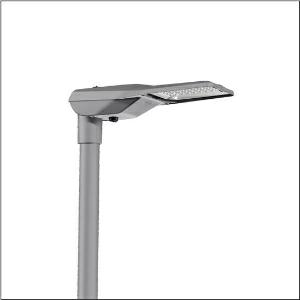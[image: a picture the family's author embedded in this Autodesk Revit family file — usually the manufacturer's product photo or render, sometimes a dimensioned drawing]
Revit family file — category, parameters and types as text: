
# Revit family: streetlight_sl_21_iq_mini___st1_0ab_5xe2m31y08gb_c9fc
name_source: partatom
category: Lighting Fixtures
units: mm (PartAtom-declared; Revit-internal decimal feet)

## family parameters
Cut with Voids When Loaded = No
Host = Face
Light Source = No
Part Type = Normal
Room Calculation Point = No
Round Connector Dimension = Use Diameter
Shared = No

## types (1)
- --- (1 x LED, 5270 lm, 39.8 W, 3000K)
    Apparent Load = 40 VA
    CIE Flux Codes = 38 73 97 100 100
    Color Rendering = 70
    Color Temperature = 3000K
    Default Elevation = 1800 mm
    Description = Streetlight SL 21 iQ mini, mast luminaire, primary light control with lens, of PMMA, primary optical cover: cover, of toughened safety glass, transparent, light distribution: ST1.0aB, light emission: direct distribution, primary light characteristic: asymmetric, installation type: post-top, side-entry, LED, High Power LED, rated luminous flux: 5.270lm, luminous efficacy: 132lm/W, light colour: 730, colour temperature: 3000K, control: presetting dimming logarithmic, Street-Remote, Auto-Match, Temp-Guard, Lumen-Switch, Night-Set, Smart-Wire, Light-Fading, Desk-Remote (wireless, voltage-free reading and setting of iQ features in the workshop via application-optimized NFC function/RFID function), optimised constant luminous flux control (CLO 2.0), mains connection: 220..240V, AC, 50/60Hz, start of lifetime: 40W, end of service life: 41W, reduction: 18W, luminaire housing, of diecast aluminium, powder-coated, Siteco® metallic grey (DB 702S), corrosivity category C5 mid according to DIN EN ISO 12944, please order mast flange separately, inclination adjustable: 0°, 5°, 10°, 15°, sealing non-destructively replaceable, multi-level sealing system, length: 628mm, width: 235mm, height: 110mm, mast flange for spigot size: 42mm (side-entry): 5XC10008XM4, 60/48mm (side-entry/post-top): 5XC10108XM2, 76/60mm (side-entry/post-top): 5XC10108XM1, Smart Interface below and above, protection rating (complete): IP66, insulation class (complete): insulation class II (safety insulation), certification: CE, ENEC, ENEC+, VDE, impact resistance: IK09, permissible operating ambient temperature for outdoor applications: -40..+50°C, standard-compliant lighting for roads and squares, packaging unit: 1 piece

Light Distribution: ST1.0aB
    Height = 110 mm
    Lamp = 1 x LED
    Lamp Light Flux = 5270 lm
    Lamp Power = 39.8 W
    Lamp count = 1
    Length = 625 mm
    Luminous efficacy = 132 lm/W
    Manufacturer = Siteco
    ModVariant = No
    Model = 5XE2M31Y08GB
    Number of Poles = 1
    OnlyDefault = Yes
    Power Factor = 1
    Product Name = Streetlight SL 21 iQ mini | ST1.0aB
    Product group = mast luminaire | pylon top
    ProductGroupID = 6100
    Protection Class = Protection class II
    Protection Degree = IP 66
    RLX_Detail_Level = 1
    RLX_Emergency_Light_Flux = 0 lm
    RLX_Emergency_Type = 0
    RLX_Emergency_Type_DB = No
    RlxData = <blob elided: 92677 chars, md5=9fed7d49>
    Socket = socket
    Standby Power = 0 W
    System Light Flux = 5270 lm
    System Power = 40 W
    Type Comments = factory setting: luminous flux: 100 % | dim-lin: 254 | 800 mA
    Type Image = l_1003514.jpg
    URL = http://relux.com
    VarID = @adj_060679
    Voltage = 0 V
    Weight = 0.00 kg
    Width = 234 mm

## geometry (parser evidence)
native form markers: Blend x4, Sweep x11
no freeform markers — native parametric forms only
